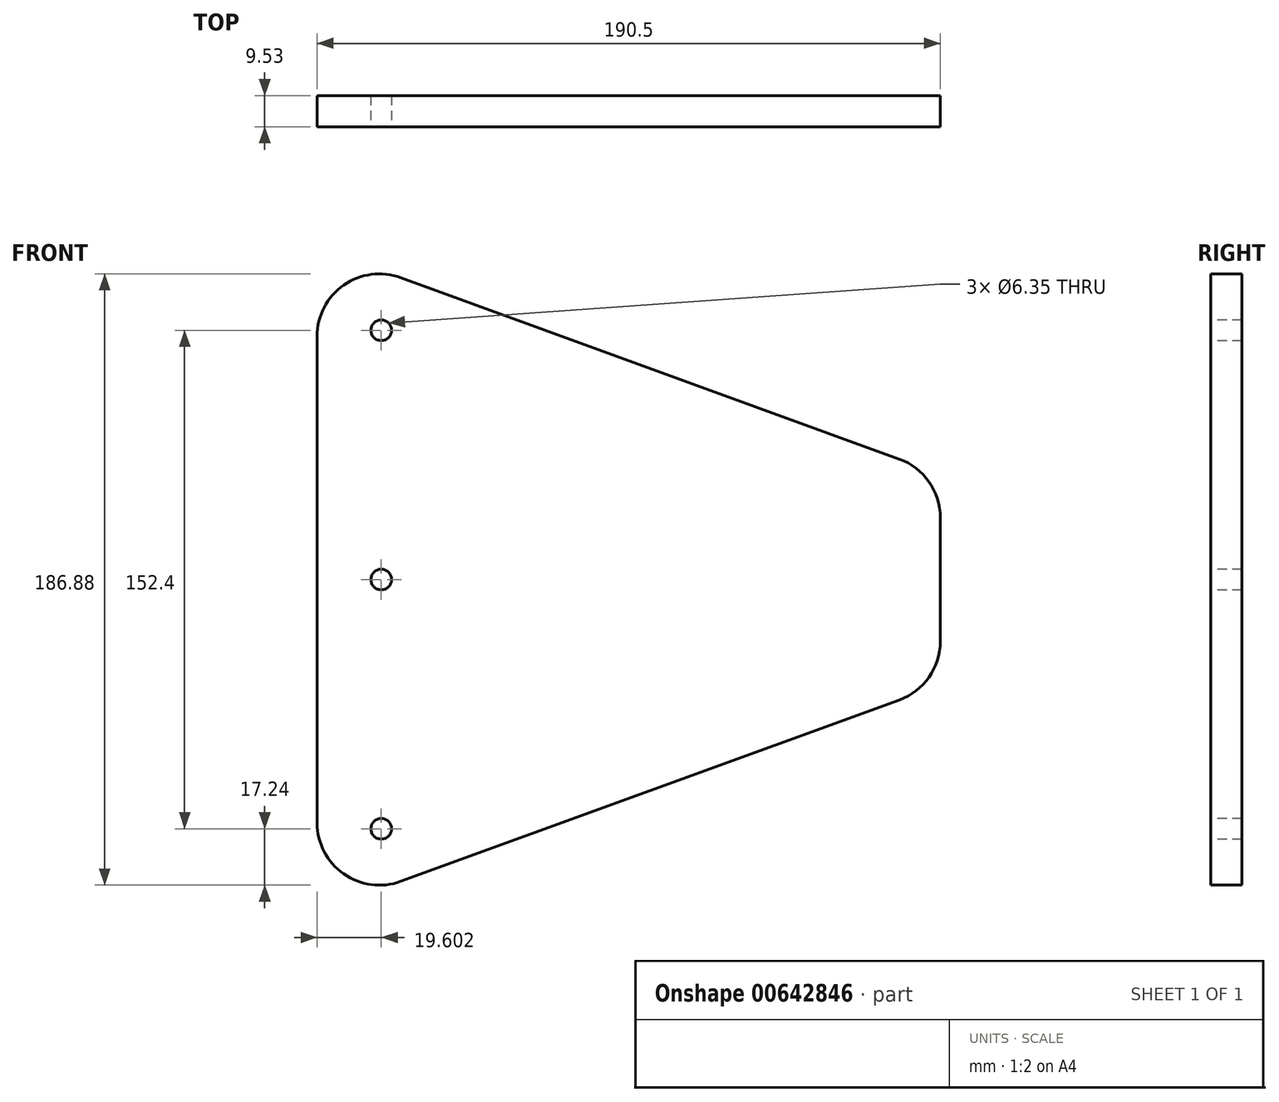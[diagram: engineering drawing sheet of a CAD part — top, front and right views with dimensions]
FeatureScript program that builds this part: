
annotation { "Feature Type Name" : "Feature", "Feature Type Description" : "" }
export const myFeature = defineFeature(function(context is Context, id is Id, definition is map)
    precondition{}
    {
        {
            var Q0;
            Q0=qCreatedBy(makeId("Front.planeOp"),FACE);
            var sketch = newSketch(context, id + "F0", { "sketchPlane" : qUnion([Q0])});
            skLineSegment(sketch, "E0", {"start": v(0, 27.2) * mm, "end": v(0, 176) * mm});
            skLineSegment(sketch, "E1", {"start": v(25.57, 193.9) * mm, "end": v(177.97, 138.43) * mm});
            skLineSegment(sketch, "E2", {"start": v(190.5, 120.52) * mm, "end": v(190.5, 82.68) * mm});
            skLineSegment(sketch, "E3", {"start": v(177.97, 64.77) * mm, "end": v(25.57, 9.3) * mm});
            skPoint(sketch, "E4.endSnap0", {"position": v(0, 101.6) * mm});
            skPoint(sketch, "E5", {"position": v(190.5, 101.6) * mm});
            skPoint(sketch, "E6.visualSharp", {"position": v(0, 203.2) * mm});
            skArc(sketch, "E6.filletArc", {"start": v(25.57, 193.9) * mm, "mid": v(8.12, 191.6) * mm, "end": v(0, 176) * mm});
            skPoint(sketch, "E7.visualSharp", {"position": v(0, 0) * mm});
            skArc(sketch, "E7.filletArc", {"start": v(0, 27.2) * mm, "mid": v(8.12, 11.6) * mm, "end": v(25.57, 9.3) * mm});
            skPoint(sketch, "E8.visualSharp", {"position": v(190.5, 133.86) * mm});
            skArc(sketch, "E8.filletArc", {"start": v(190.5, 120.52) * mm, "mid": v(187.05, 131.45) * mm, "end": v(177.97, 138.43) * mm});
            skPoint(sketch, "E9.visualSharp", {"position": v(190.5, 69.34) * mm});
            skArc(sketch, "E9.filletArc", {"start": v(177.97, 64.77) * mm, "mid": v(187.05, 71.75) * mm, "end": v(190.5, 82.68) * mm});
            skSolve(sketch);
        }
        {
            var Q0;
            Q0 = qSketchRegion(id + "F0", true);
            extrude(context, id + "F1", {"entities" : qUnion([Q0]), "depth" : 9.52 * mm, "offsetDistance" : 25.4 * mm});
        }
        {
            var Q0;
            Q0=makeQuery(id+"F1.opExtrude","CAP_FACE",FACE,{"disambiguationData":[OSD([sQuery(id+"F0.wireOp",EDGE,"E0"),sQuery(id+"F0.wireOp",EDGE,"E1"),sQuery(id+"F0.wireOp",EDGE,"E2"),sQuery(id+"F0.wireOp",EDGE,"E3"),sQuery(id+"F0.wireOp",EDGE,"E6.filletArc"),sQuery(id+"F0.wireOp",EDGE,"E7.filletArc"),sQuery(id+"F0.wireOp",EDGE,"E8.filletArc"),sQuery(id+"F0.wireOp",EDGE,"E9.filletArc")])],"isStart":false});
            var sketch = newSketch(context, id + "F2", { "sketchPlane" : qUnion([Q0])});
            skCircle(sketch, "E10", {"center": v(19.6, 177.8) * mm, "radius": 13.5 * mm});
            skCircle(sketch, "E11", {"center": v(19.6, 101.6) * mm, "radius": 10.32 * mm});
            skCircle(sketch, "E12", {"center": v(19.6, 25.4) * mm, "radius": 13.5 * mm});
            skSolve(sketch);
        }
        {
            var Q0;
            Q0=sQuery(id+"F2.wireOp",VERTEX,"E10.center");
            var Q1;
            Q1=sQuery(id+"F2.wireOp",VERTEX,"E11.center");
            var Q2;
            Q2=sQuery(id+"F2.wireOp",VERTEX,"E12.center");
            var Q3;
            Q3=makeQuery(id+"F1.opExtrude","SWEPT_BODY",BODY,{"disambiguationData":[OSD([sQuery(id+"F0.wireOp",EDGE,"E0"),sQuery(id+"F0.wireOp",EDGE,"E1"),sQuery(id+"F0.wireOp",EDGE,"E2"),sQuery(id+"F0.wireOp",EDGE,"E3"),sQuery(id+"F0.wireOp",EDGE,"E6.filletArc"),sQuery(id+"F0.wireOp",EDGE,"E7.filletArc"),sQuery(id+"F0.wireOp",EDGE,"E8.filletArc"),sQuery(id+"F0.wireOp",EDGE,"E9.filletArc")])]});
            hole(context, id + "F3", {"style" : HoleStyle.SIMPLE, "endStyle" : HoleEndStyle.THROUGH, "holeDiameter" : 6.35 * mm, "majorDiameter" : 6.35 * mm, "isTappedThrough" : true, "tappedDepth" : 12.7 * mm, "tapClearance" : 3, "locations" : qUnion([Q0, Q1, Q2]), "scope" : qUnion([Q3])});
        }
    });
